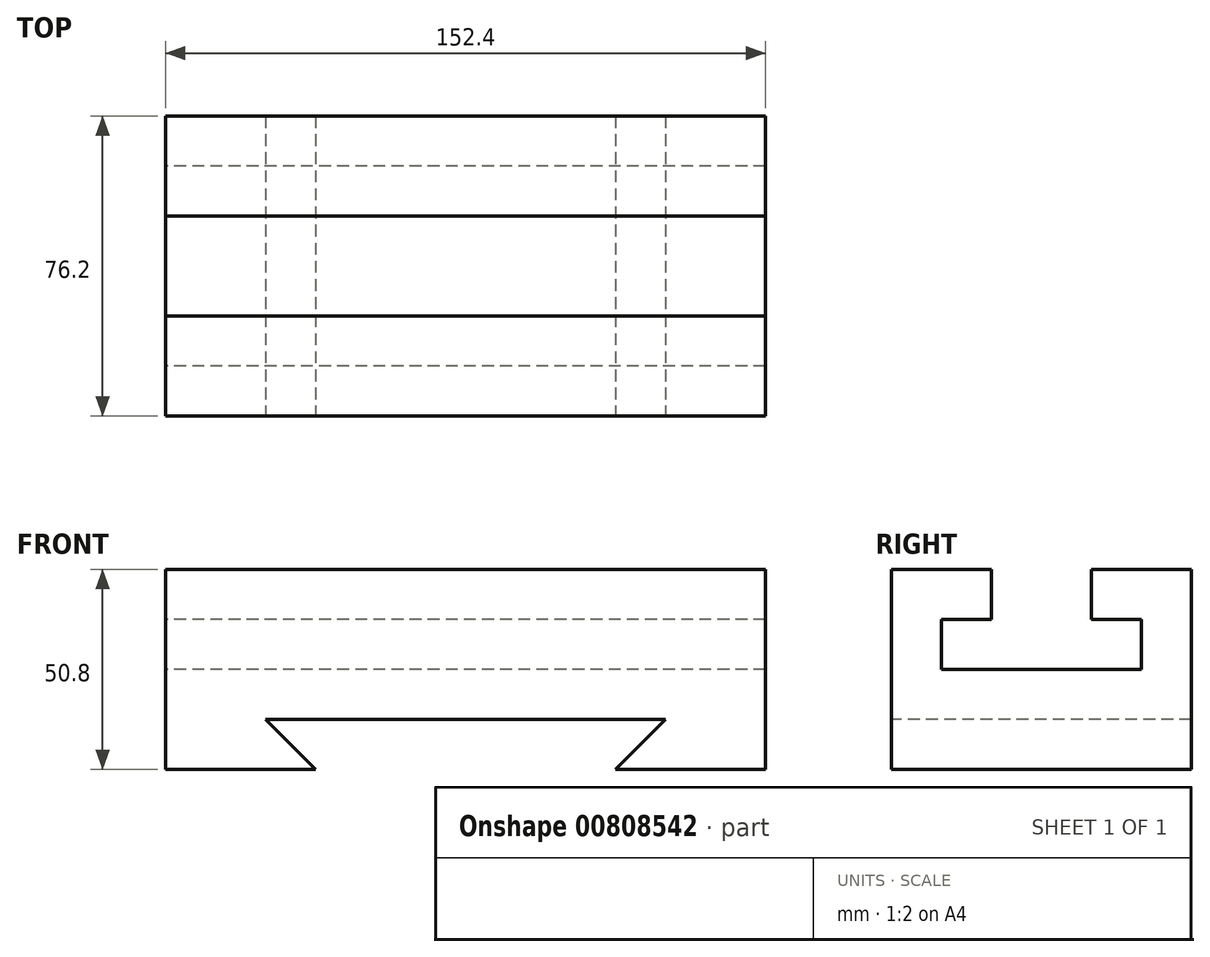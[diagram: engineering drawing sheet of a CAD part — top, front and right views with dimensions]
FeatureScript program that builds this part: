
annotation { "Feature Type Name" : "Feature", "Feature Type Description" : "" }
export const myFeature = defineFeature(function(context is Context, id is Id, definition is map)
    precondition{}
    {
        {
            var Q0;
            Q0=qCreatedBy(makeId("Right.planeOp"),FACE);
            var sketch = newSketch(context, id + "F0", { "sketchPlane" : qUnion([Q0])});
            skLineSegment(sketch, "E0", {"start": v(-25.4, 0) * mm, "end": v(-25.4, -12.7) * mm});
            skLineSegment(sketch, "E1", {"start": v(-25.4, -12.7) * mm, "end": v(-38.1, -12.7) * mm});
            skLineSegment(sketch, "E2", {"start": v(-38.1, -12.7) * mm, "end": v(-38.1, -25.4) * mm});
            skLineSegment(sketch, "E3", {"start": v(-38.1, -25.4) * mm, "end": v(12.7, -25.4) * mm});
            skLineSegment(sketch, "E4", {"start": v(12.7, -25.4) * mm, "end": v(12.7, -12.7) * mm});
            skLineSegment(sketch, "E5", {"start": v(12.7, -12.7) * mm, "end": v(0, -12.7) * mm});
            skLineSegment(sketch, "E6", {"start": v(0, -12.7) * mm, "end": v(0, 0) * mm});
            skLineSegment(sketch, "E7", {"start": v(0, 0) * mm, "end": v(25.4, 0) * mm});
            skLineSegment(sketch, "E8", {"start": v(25.4, 0) * mm, "end": v(25.4, -50.8) * mm});
            skLineSegment(sketch, "E9", {"start": v(25.4, -50.8) * mm, "end": v(-50.8, -50.8) * mm});
            skLineSegment(sketch, "E10", {"start": v(-50.8, -50.8) * mm, "end": v(-50.8, 0) * mm});
            skLineSegment(sketch, "E11", {"start": v(-50.8, 0) * mm, "end": v(-25.4, 0) * mm});
            skSolve(sketch);
        }
        {
            var Q0;
            Q0 = qSketchRegion(id + "F0", true);
            extrude(context, id + "F1", {"entities" : qUnion([Q0]), "depth" : 152.4 * mm, "offsetDistance" : 25.4 * mm});
        }
        {
            var Q0;
            Q0=makeQuery(id+"F1.opExtrude","SWEPT_FACE",FACE,{"disambiguationData":[OSD([sQuery(id+"F0.wireOp",EDGE,"E10")])]});
            var sketch = newSketch(context, id + "F2", { "sketchPlane" : qUnion([Q0])});
            skLineSegment(sketch, "E12", {"start": v(38.1, -50.8) * mm, "end": v(25.4, -38.1) * mm});
            skLineSegment(sketch, "E13", {"start": v(25.4, -38.1) * mm, "end": v(127, -38.1) * mm});
            skLineSegment(sketch, "E14", {"start": v(127, -38.1) * mm, "end": v(114.3, -50.8) * mm});
            skSolve(sketch);
        }
        {
            var Q0;
            {var subQ0=sQuery(id+"F2.wireOp",EDGE,"E12");Q0=makeQuery(id+"F2.imprint","IMPRINT",FACE,{"disambiguationData":[TD([[makeQuery(id+"F2.imprint","IMPRINT",EDGE,{"derivedFrom":subQ0}),-1.0]])]});}
            extrude(context, id + "F3", {"entities" : qUnion([Q0]), "operationType" : NewBodyOperationType.REMOVE, "endBound" : BoundingType.THROUGH_ALL, "oppositeDirection" : true, "depth" : 25.4 * mm, "offsetDistance" : 25.4 * mm});
        }
    });
